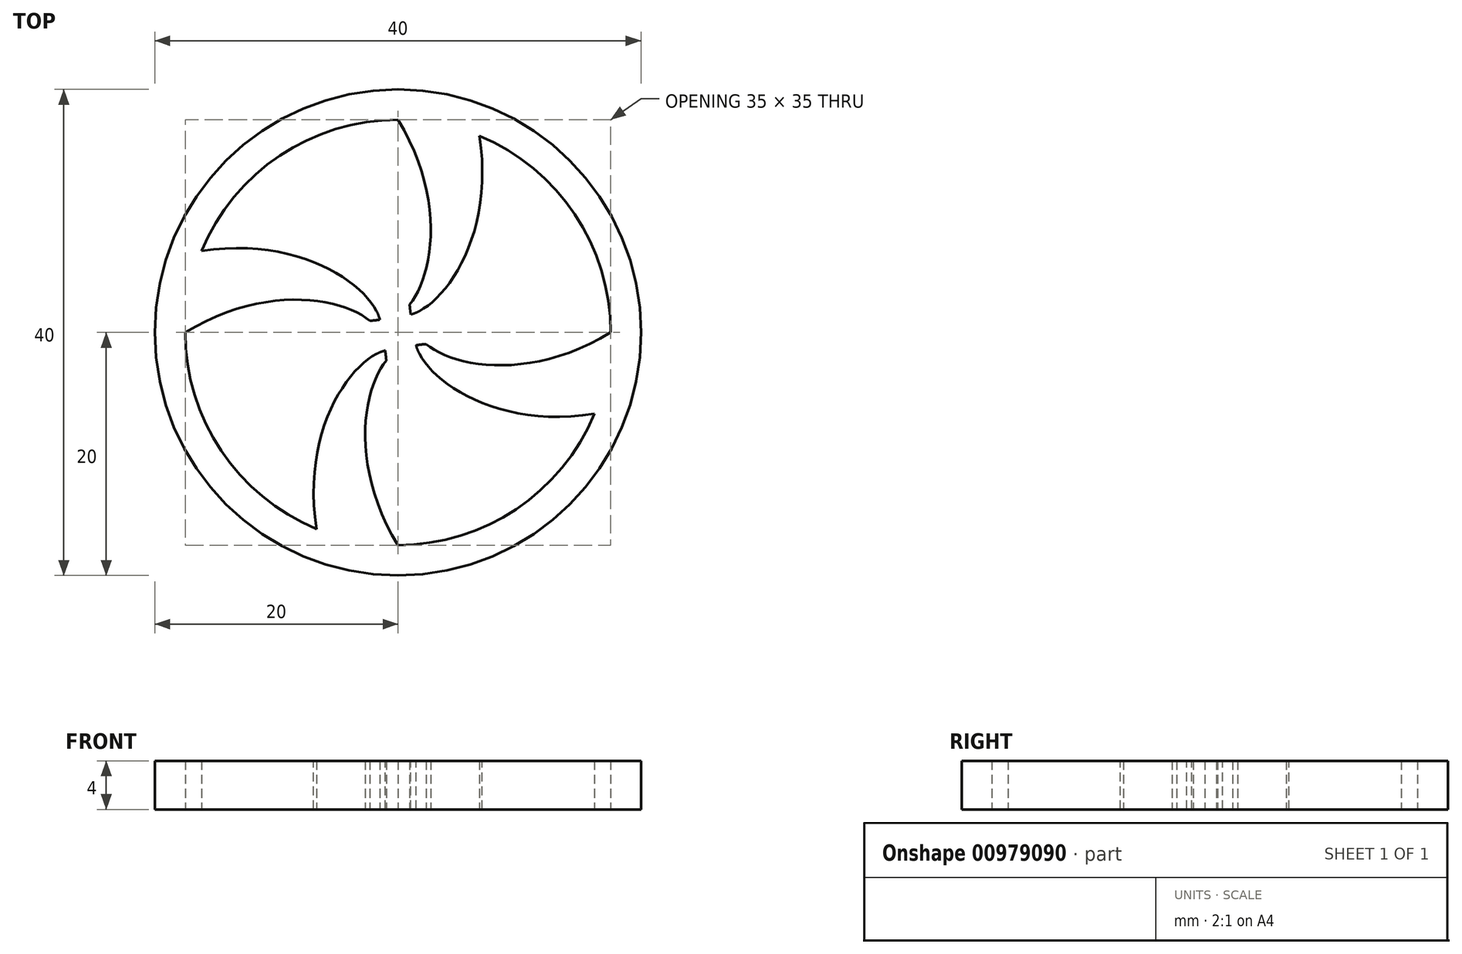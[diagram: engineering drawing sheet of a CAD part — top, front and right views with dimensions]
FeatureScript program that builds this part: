
annotation { "Feature Type Name" : "Feature", "Feature Type Description" : "" }
export const myFeature = defineFeature(function(context is Context, id is Id, definition is map)
    precondition{}
    {
        {
            var Q0;
            Q0=qCreatedBy(makeId("Top.planeOp"),FACE);
            var sketch = newSketch(context, id + "F0", { "sketchPlane" : qUnion([Q0])});
            skCircle(sketch, "E0", {"center": v(0, 0) * mm, "radius": 20 * mm});
            skArc(sketch, "E1", {"start": v(0, 17.5) * mm, "mid": v(-9.72, 14.55) * mm, "end": v(-16.17, 6.7) * mm});
            skFitSpline(sketch, "E2", {"points": [v(0, 17.5) * mm, v(0.96, 2.3) * mm, v(-2.3, 0.96) * mm], "startDerivative": vector(17.94, -29.36) * mm, "endDerivative": vector(-11.9, -1.18) * mm});
            skFitSpline(sketch, "E3", {"points": [v(6.7, 16.17) * mm, v(1.77, 1.77) * mm, v(-1.77, 1.77) * mm], "startDerivative": vector(5.33, -34) * mm, "endDerivative": vector(-11.45, 3.47) * mm});
            skFitSpline(sketch, "E4", {"points": [v(0, -17.5) * mm, v(-0.96, -2.3) * mm, v(2.3, -0.96) * mm], "startDerivative": vector(-17.94, 29.36) * mm, "endDerivative": vector(11.9, 1.18) * mm});
            skFitSpline(sketch, "E5", {"points": [v(-6.7, -16.17) * mm, v(-1.77, -1.77) * mm, v(1.77, -1.77) * mm], "startDerivative": vector(-5.33, 34) * mm, "endDerivative": vector(11.45, -3.47) * mm});
            skFitSpline(sketch, "E6", {"points": [v(17.5, 0) * mm, v(2.3, -0.96) * mm, v(0.96, 2.3) * mm], "startDerivative": vector(-29.36, -17.94) * mm, "endDerivative": vector(-1.18, 11.9) * mm});
            skFitSpline(sketch, "E7", {"points": [v(16.17, -6.7) * mm, v(1.77, -1.77) * mm, v(1.77, 1.77) * mm], "startDerivative": vector(-34, -5.33) * mm, "endDerivative": vector(3.47, 11.45) * mm});
            skFitSpline(sketch, "E8", {"points": [v(-17.5, 0) * mm, v(-2.3, 0.96) * mm, v(-0.96, -2.3) * mm], "startDerivative": vector(29.36, 17.94) * mm, "endDerivative": vector(1.18, -11.9) * mm});
            skFitSpline(sketch, "E9", {"points": [v(-16.17, 6.7) * mm, v(-1.77, 1.77) * mm, v(-1.77, -1.77) * mm], "startDerivative": vector(34, 5.33) * mm, "endDerivative": vector(-3.47, -11.45) * mm});
            skArc(sketch, "E10", {"start": v(2.3, -0.96) * mm, "mid": v(2.45, 0.49) * mm, "end": v(1.77, 1.77) * mm});
            skArc(sketch, "E11.trimOffspring", {"start": v(0.96, 2.3) * mm, "mid": v(-0.49, 2.45) * mm, "end": v(-1.77, 1.77) * mm});
            skArc(sketch, "E12.trimOffspring", {"start": v(-2.3, 0.96) * mm, "mid": v(-2.45, -0.49) * mm, "end": v(-1.77, -1.77) * mm});
            skArc(sketch, "E13.trimOffspring", {"start": v(-0.96, -2.3) * mm, "mid": v(0.49, -2.45) * mm, "end": v(1.77, -1.77) * mm});
            skArc(sketch, "E14.trimOffspring", {"start": v(-17.5, 0) * mm, "mid": v(-14.55, -9.72) * mm, "end": v(-6.7, -16.17) * mm});
            skArc(sketch, "E15.trimOffspring", {"start": v(0, -17.5) * mm, "mid": v(9.72, -14.55) * mm, "end": v(16.17, -6.7) * mm});
            skArc(sketch, "E16.trimOffspring", {"start": v(17.5, 0) * mm, "mid": v(14.55, 9.72) * mm, "end": v(6.7, 16.17) * mm});
            skCircle(sketch, "E17", {"center": v(0, 0) * mm, "radius": 0.9 * mm});
            skSolve(sketch);
        }
        {
            var Q0;
            Q0=makeQuery(id+"F0.imprint","IMPRINT",FACE,{"disambiguationData":[TD([[makeQuery(id+"F0.imprint","IMPRINT",EDGE,{"derivedFrom":sQuery(id+"F0.wireOp",EDGE,"E0")}),1.0]])]});
            extrude(context, id + "F1", {"entities" : qUnion([Q0]), "depth" : 4 * mm, "offsetDistance" : 25 * mm});
        }
    });
